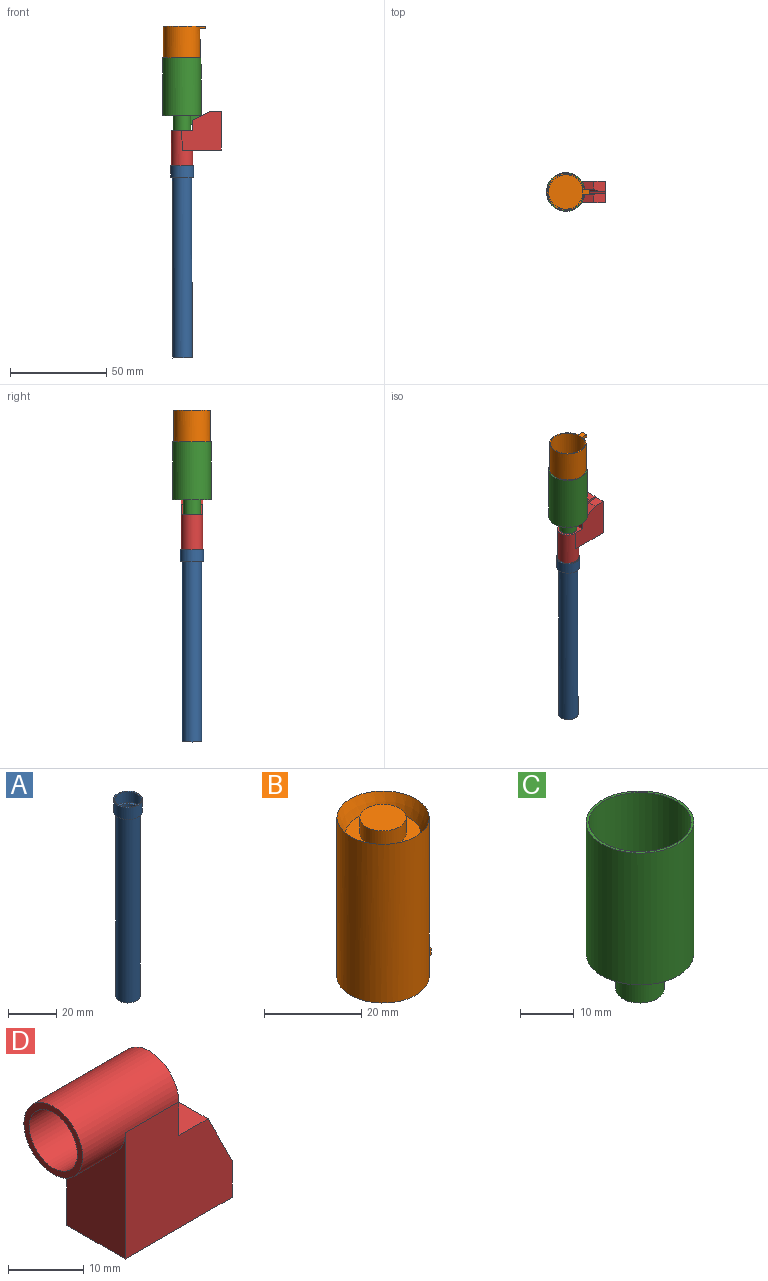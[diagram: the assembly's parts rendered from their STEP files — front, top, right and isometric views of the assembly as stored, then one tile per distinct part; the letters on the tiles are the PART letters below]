
ASSEMBLY  parts=4 mates=3
PART A: 8 faces, bbox 12x12x100 mm
  f0: plane 12x12mm, normal (0,0,1), area 18.1mm2, adj f1,f7
  f1: cylinder r=5.5mm len=11mm, axis (0,0,-1), area 190.1mm2, adj f0,f2
  f2: plane 11x11mm, normal (0,0,1), area 31.4mm2, adj f1,f3
  f3: cylinder r=4.5mm len=94.5mm, axis (0,0,-1), area 2671.9mm2, adj f2,f4
  f4: plane 10x10mm, normal (0,0,-1), area 14.9mm2, adj f3,f5
  f5: cylinder r=5mm len=94mm, axis (0,0,-1), area 2953.1mm2, adj f4,f6
  f6: plane 12x12mm, normal (0,0,-1), area 34.6mm2, adj f5,f7
  f7: cylinder r=6mm len=12mm, axis (0,0,-1), area 226.2mm2, adj f0,f6
PART B: 12 faces, bbox 22x19x40 mm
  f0: plane 3.12x1.5mm, normal (0,-1,0), area 4.7mm2, adj f2,f3,f4,f9
  f1: plane 3.12x1.5mm, normal (0,1,0), area 4.7mm2, adj f2,f3,f4,f9
  f2: plane 3.12x3mm, normal (0,0,1), area 9.1mm2, adj f0,f1,f4,f9
  f3: plane 22x19mm, normal (0,0,-1), area 38.2mm2, adj f0,f1,f4,f8,f9
  f4: plane 3x1.5mm, normal (1,0,0), area 4.5mm2, adj f0,f1,f2,f3
  f5: cylinder r=4.75mm len=9.5mm, axis (0,0,1), area 119.4mm2, adj f6,f11
  f6: plane 9.5x9.5mm, normal (0,0,1), area 70.9mm2, adj f5
  f7: plane 18x18mm, normal (0,0,-1), area 254.5mm2, adj f8
  f8: cylinder r=9mm len=35mm, axis (0,0,1), area 1979.2mm2, adj f3,f7
  f9: cylinder r=9.5mm len=40mm, axis (0,0,1), area 2383.1mm2, adj f0,f1,f2,f3,f10
  f10: cone r=7.75mm half-angle=23.6deg, axis (0,0,1), area 236.6mm2, adj f9,f11
  f11: plane 15.5x15.5mm, normal (0,0,1), area 117.8mm2, adj f5,f10
PART C: 16 faces, bbox 22x20x38 mm
  f0: cylinder r=4.5mm len=9mm, axis (0,0,-1), area 222.2mm2, adj f1,f7,f8,f9,f13
  f1: plane 20x20mm, normal (0,0,-1), area 247.8mm2, adj f0,f2,f8,f9
  f2: cylinder r=10mm len=30mm, axis (0,0,-1), area 1884.7mm2, adj f1,f3,f9,f11,f12
  f3: plane 20x20mm, normal (0,0,1), area 30.6mm2, adj f2,f4
  f4: cylinder r=9.5mm len=29.5mm, axis (0,0,-1), area 1760.9mm2, adj f3,f5
  f5: plane 19x19mm, normal (0,0,1), area 233.3mm2, adj f4,f6
  f6: cylinder r=4mm len=8.5mm, axis (0,0,-1), area 213.6mm2, adj f5,f7
  f7: plane 9x9mm, normal (0,0,-1), area 13.4mm2, adj f0,f6,f9,f13
  f8: plane 7.5x5mm, normal (0,1,0), area 26.2mm2, adj f0,f1,f10,f14,f15
  f9: plane 8.5x7.53mm, normal (0,-1,0), area 26.5mm2, adj f0,f1,f2,f7,f10,f11,f12,f13
  f10: plane 2x0.5mm, normal (0,0,1), area 1mm2, adj f8,f9,f11,f15
  f11: plane 0.5x0.5mm, normal (1,0,0), area 0.3mm2, adj f2,f9,f10,f12
  f12: plane 0.5x0.01mm, normal (0,0,1), area 0mm2, adj f2,f9,f11
  f13: plane 3x0.5mm, normal (1,0,0), area 1.5mm2, adj f0,f7,f9,f14
  f14: plane 7.5x3mm, normal (0.37,0,-0.93), area 4mm2, adj f8,f9,f13,f15
  f15: plane 2x0.5mm, normal (1,0,0), area 1mm2, adj f8,f9,f10,f14
PART D: 18 faces, bbox 28x11x26 mm
  f0: plane 20x11mm, normal (0,0,-1), area 219.6mm2, adj f1,f3,f7,f8,f9,f12,f13,f15
  f1: plane 6x5mm, normal (1,0,0), area 28.9mm2, adj f0,f2,f9,f13,f16
  f2: plane 11x9mm, normal (0.89,0,0.45), area 81.9mm2, adj f1,f3,f4,f8,f9,f14,f16,f17
  f3: plane 6x5mm, normal (1,0,0), area 28.9mm2, adj f0,f2,f8,f12,f17
  f4: plane 11x5.5mm, normal (0,0,1), area 60.5mm2, adj f2,f5,f8,f9
  f5: plane 11x11mm, normal (1,0,0), area 44.4mm2, adj f4,f8,f9,f10,f11
  f6: plane 11x11mm, normal (-1,0,0), area 31.4mm2, adj f10,f11
  f7: plane 20.5x11mm, normal (-1,0,0), area 178mm2, adj f0,f8,f9,f10
  f8: plane 20.5x20mm, normal (0,-1,0), area 334.8mm2, adj f0,f2,f3,f4,f5,f7,f10
  f9: plane 20.5x20mm, normal (0,1,0), area 334.8mm2, adj f0,f1,f2,f4,f5,f7,f10
  f10: cylinder r=5.5mm len=18mm, axis (1,0,0), area 449.2mm2, adj f5,f6,f7,f8,f9
  f11: cylinder r=4.5mm len=18mm, axis (-1,0,0), area 508.9mm2, adj f5,f6
  f12: plane 14.15x6.98mm, normal (0,1,0), area 27.1mm2, adj f0,f3,f14,f15,f17
  f13: plane 14.15x6.98mm, normal (0,-1,0), area 27.1mm2, adj f0,f1,f14,f15,f16
  f14: plane 3x2.68mm, normal (0.45,0,-0.89), area 4mm2, adj f2,f12,f13,f15,f16,f17
  f15: plane 13.25x6.63mm, normal (0.89,0,0.45), area 14.8mm2, adj f0,f12,f13,f14
  f16: plane 10.83x5.19mm, normal (0.63,-0.71,0.32), area 15mm2, adj f1,f2,f13,f14
  f17: plane 10.83x5.19mm, normal (0.63,0.71,0.32), area 15mm2, adj f2,f3,f12,f14
PLACE A rot(axis=(0,-1,0),0.2deg) t=(-8.93,-4.58,-103.94)mm
PLACE B rot(axis=(1,0,0),180deg) t=(-9.13,-4.58,-31.47)mm
PLACE C rot(axis=(0,-1,0),0.2deg) t=(-9.08,-4.58,-47.94)mm
PLACE D rot(axis=(0,-1,0),90.2deg) t=(-3.43,-4.58,-103.92)mm
MATE slider C.f0 <-> B.f5  axis (0,0,-1) through (-9.04,-4.58,-62.69)mm
MATE fastened C.f0 <-> D.f10  axis (0,0,-1) through (-8.98,-4.58,-85.94)mm
MATE fastened D.f10 <-> A.f1  axis (0,0,-1) through (-8.93,-4.58,-103.94)mm
